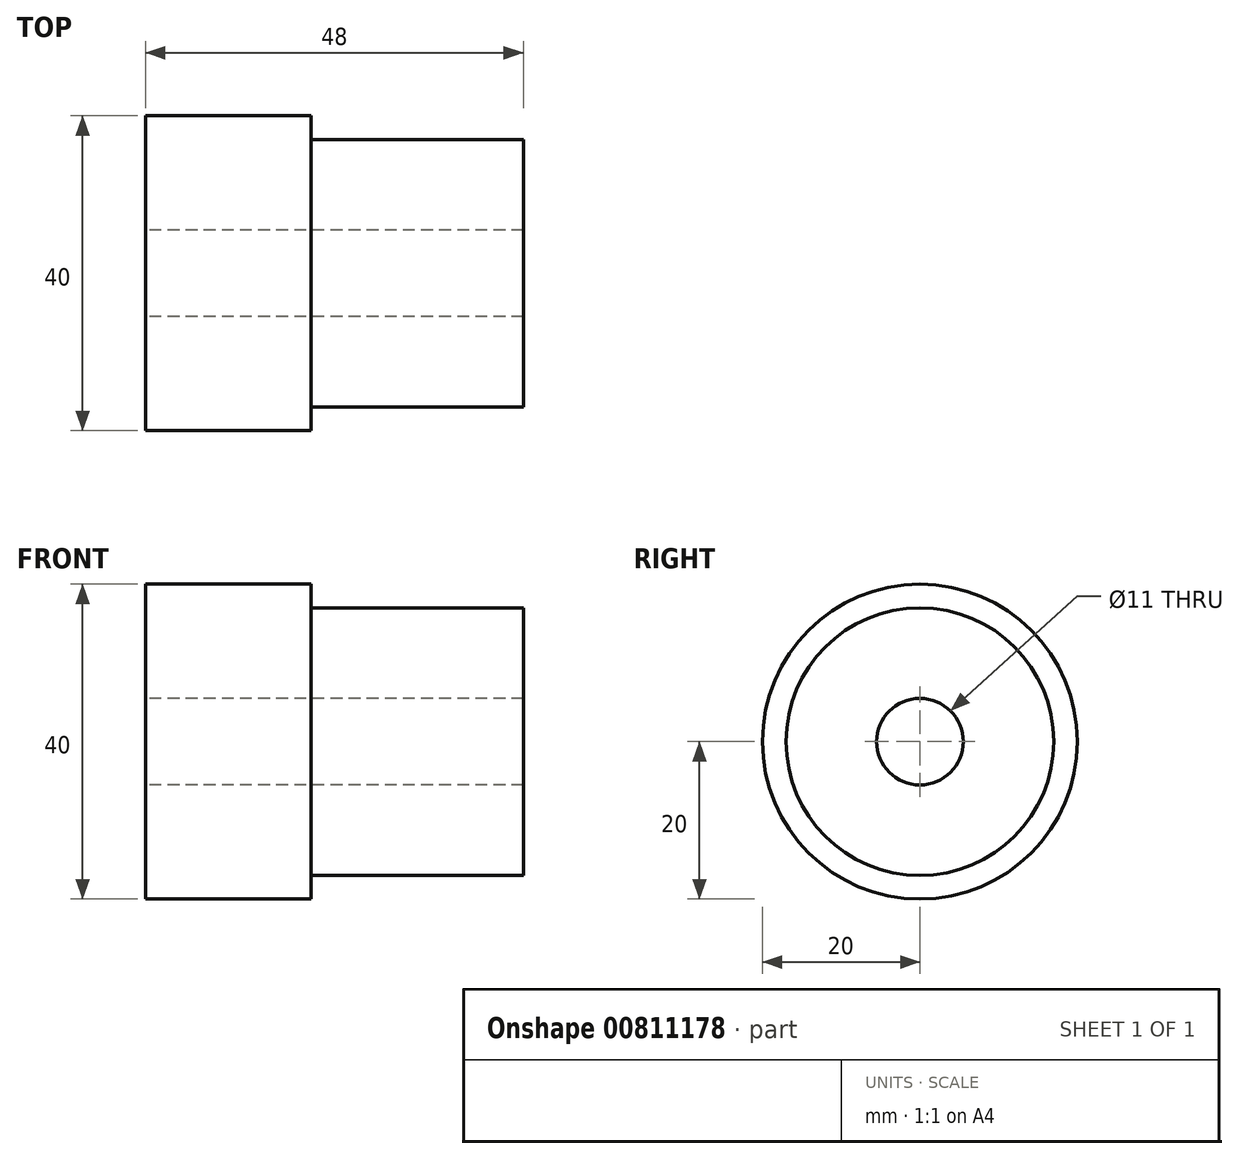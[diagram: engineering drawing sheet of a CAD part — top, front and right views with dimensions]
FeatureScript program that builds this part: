
annotation { "Feature Type Name" : "Feature", "Feature Type Description" : "" }
export const myFeature = defineFeature(function(context is Context, id is Id, definition is map)
    precondition{}
    {
        {
            var Q0;
            Q0=qCreatedBy(makeId("Front.planeOp"),FACE);
            var sketch = newSketch(context, id + "F0", { "sketchPlane" : qUnion([Q0])});
            skLineSegment(sketch, "E0.bottom", {"start": v(-24, 20) * mm, "end": v(-3, 20) * mm});
            skLineSegment(sketch, "E0.top", {"start": v(-24, -20) * mm, "end": v(24, -20) * mm});
            skLineSegment(sketch, "E0.left", {"start": v(-24, 20) * mm, "end": v(-24, 5.5) * mm});
            skLineSegment(sketch, "E0.right", {"start": v(24, 17) * mm, "end": v(24, 5.5) * mm});
            skPoint(sketch, "E0.middle", {"position": v(0, 0) * mm});
            skLineSegment(sketch, "E1", {"start": v(-70.87, 0) * mm, "end": v(64.56, 0) * mm, "construction": true});
            skLineSegment(sketch, "E2", {"start": v(-3, 20) * mm, "end": v(-3, 17) * mm});
            skLineSegment(sketch, "E3", {"start": v(-3, 17) * mm, "end": v(24, 17) * mm});
            skLineSegment(sketch, "E4", {"start": v(-24, 5.5) * mm, "end": v(24, 5.5) * mm});
            skPoint(sketch, "E5.orphan", {"position": v(24, 20) * mm});
            skLineSegment(sketch, "E6.trimOffspring", {"start": v(-24, 0) * mm, "end": v(-24, -20) * mm});
            skLineSegment(sketch, "E7.trimOffspring", {"start": v(24, 0) * mm, "end": v(24, -20) * mm});
            skLineSegment(sketch, "E8", {"start": v(24, 17) * mm, "end": v(24, 42.13) * mm, "construction": true});
            skLineSegment(sketch, "E9", {"start": v(8, 17) * mm, "end": v(8, 40.43) * mm, "construction": true});
            skLineSegment(sketch, "E10", {"start": v(24, 27.5) * mm, "end": v(-24, 27.5) * mm, "construction": true});
            skSolve(sketch);
        }
        {
            var Q0;
            Q0=makeQuery(id+"F0.imprint","IMPRINT",FACE,{"disambiguationData":[TD([[makeQuery(id+"F0.imprint","IMPRINT",EDGE,{"derivedFrom":sQuery(id+"F0.wireOp",EDGE,"E0.bottom")}),-1.0]])]});
            var Q1;
            Q1=sQuery(id+"F0.wireOp",EDGE,"E1");
            revolve(context, id + "F1", {"surfaceOperationType" : NewSurfaceOperationType.NEW, "entities" : qUnion([Q0]), "axis" : qUnion([Q1]), "revolveType" : RevolveType.FULL});
        }
    });
